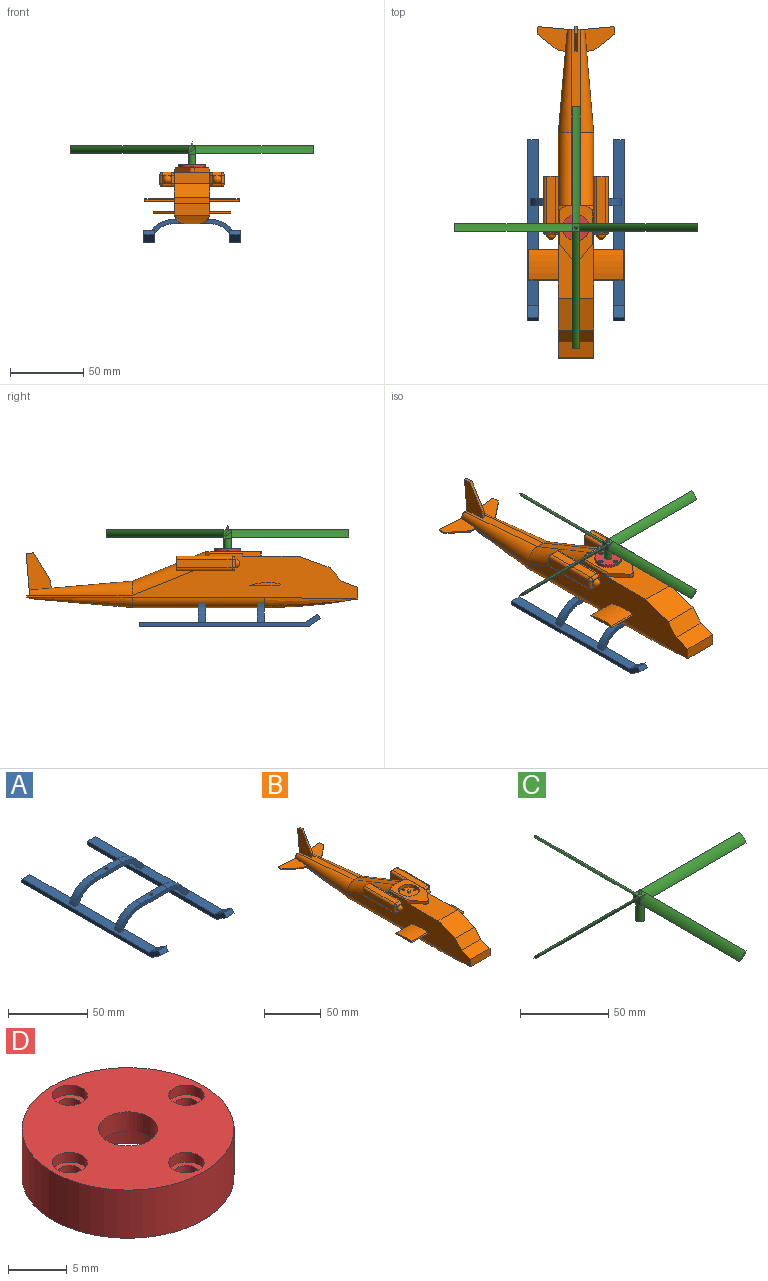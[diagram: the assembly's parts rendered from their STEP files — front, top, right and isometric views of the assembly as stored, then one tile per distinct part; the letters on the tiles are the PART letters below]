
ASSEMBLY  parts=4 mates=3
PART A: 38 faces, bbox 65.5x123.3x16 mm
  f0: cylinder r=20mm len=18.74mm, axis (0,-1,0), area 121.3mm2, adj f1,f6,f7,f8
  f1: plane 24x5mm, normal (0,0,1), area 116.9mm2, adj f0,f2,f6,f7,f35
  f2: cylinder r=20mm len=18.74mm, axis (0,-1,0), area 121.3mm2, adj f1,f6,f7,f9
  f3: cylinder r=17mm len=15.49mm, axis (0,-1,0), area 97.4mm2, adj f4,f6,f7,f9
  f4: plane 24x5mm, normal (0,0,-1), area 112.9mm2, adj f3,f5,f6,f7,f37
  f5: cylinder r=17mm len=15.49mm, axis (0,-1,0), area 97.4mm2, adj f4,f6,f7,f8
  f6: plane 61.47x13mm, normal (0,1,0), area 203.3mm2, adj f0,f1,f2,f3,f4,f5,f8,f9
  f7: plane 61.47x13mm, normal (0,-1,0), area 203.3mm2, adj f0,f1,f2,f3,f4,f5,f8,f9
  f8: plane 113x7mm, normal (0,0,1), area 758.6mm2, adj f0,f5,f6,f7,f10,f15,f16,f17
  f9: plane 113x7mm, normal (0,0,1), area 758.6mm2, adj f2,f3,f6,f7,f12,f13,f16,f17
  f10: cylinder r=20mm len=18.74mm, axis (0,1,0), area 121.3mm2, adj f8,f11,f16,f17
  f11: plane 24x5mm, normal (0,0,1), area 116.9mm2, adj f10,f12,f16,f17,f32
  f12: cylinder r=20mm len=18.74mm, axis (0,1,0), area 121.3mm2, adj f9,f11,f16,f17
  f13: cylinder r=17mm len=15.49mm, axis (0,1,0), area 97.4mm2, adj f9,f14,f16,f17
  f14: plane 24x5mm, normal (0,0,-1), area 112.9mm2, adj f13,f15,f16,f17,f34
  f15: cylinder r=17mm len=15.49mm, axis (0,1,0), area 97.4mm2, adj f8,f14,f16,f17
  f16: plane 61.47x13mm, normal (0,-1,0), area 203.3mm2, adj f8,f9,f10,f11,f12,f13,f14,f15
  f17: plane 61.47x13mm, normal (0,1,0), area 203.3mm2, adj f8,f9,f10,f11,f12,f13,f14,f15
  f18: plane 123.32x8.55mm, normal (-1,0,0), area 378.1mm2, adj f8,f19,f21,f26,f27,f28
  f19: plane 115x7mm, normal (0,0,-1), area 805mm2, adj f18,f20,f21,f26
  f20: plane 123.32x8.55mm, normal (1,0,0), area 378.1mm2, adj f8,f19,f21,f26,f27,f28
  f21: plane 7x3mm, normal (0,1,0), area 21mm2, adj f8,f18,f19,f20
  f22: plane 115x7mm, normal (0,0,-1), area 805mm2, adj f23,f24,f25,f30
  f23: plane 123.32x8.55mm, normal (1,0,0), area 378.1mm2, adj f9,f22,f25,f29,f30,f31
  f24: plane 123.32x8.55mm, normal (-1,0,0), area 378.1mm2, adj f9,f22,f25,f29,f30,f31
  f25: plane 7x3mm, normal (0,1,0), area 21mm2, adj f9,f22,f23,f24
  f26: plane 8.32x7mm, normal (0,-0.55,-0.83), area 70mm2, adj f18,f19,f20,f28
  f27: plane 8.32x7mm, normal (0,0.55,0.83), area 70mm2, adj f8,f18,f20,f28
  f28: plane 7x3mm, normal (0,-0.83,0.55), area 25.2mm2, adj f18,f20,f26,f27
  f29: plane 8.32x7mm, normal (0,0.55,0.83), area 70mm2, adj f9,f23,f24,f31
  f30: plane 8.32x7mm, normal (0,-0.55,-0.83), area 70mm2, adj f22,f23,f24,f31
  f31: plane 7x3mm, normal (0,-0.83,0.55), area 25.2mm2, adj f23,f24,f29,f30
  f32: cylinder r=1mm len=2mm, axis (0,0,-1), area 12.6mm2, adj f11,f33
  f33: plane 3x3mm, normal (0,0,-1), area 3.9mm2, adj f32,f34
  f34: cylinder r=1.5mm len=3mm, axis (0,0,-1), area 9.4mm2, adj f14,f33
  f35: cylinder r=1mm len=2mm, axis (0,0,-1), area 12.6mm2, adj f1,f36
  f36: plane 3x3mm, normal (0,0,-1), area 3.9mm2, adj f35,f37
  f37: cylinder r=1.5mm len=3mm, axis (0,0,-1), area 9.4mm2, adj f4,f36
PART B: 133 faces, bbox 65.5x239.2x39.5 mm
  f0: plane 35x10mm, normal (0,0,-1), area 350mm2, adj f2,f3,f110,f114
  f1: plane 45x10mm, normal (0,0,-1), area 450mm2, adj f2,f3,f33,f111
  f2: cylinder r=7mm len=90mm, axis (0,-1,0), area 922.2mm2, adj f0,f1,f8,f17,f32,f110,f111,f112
  f3: cylinder r=7mm len=90mm, axis (0,-1,0), area 922.2mm2, adj f0,f1,f4,f27,f34,f110,f111,f112
  f4: plane 153.65x31.31mm, normal (-1,0,0), area 3016.8mm2, adj f3,f5,f9,f11,f12,f13,f14,f27
  f5: plane 70x6.12mm, normal (-1,0.09,0), area 76.8mm2, adj f4,f34,f35,f37,f83,f84
  f6: plane 70x6.12mm, normal (0,0.09,1), area 391.6mm2, adj f24,f35,f36,f37,f72,f73,f74
  f7: plane 70x6.12mm, normal (1,0.09,0), area 76.8mm2, adj f8,f32,f36,f37,f65,f68
  f8: plane 153.65x31.31mm, normal (1,0,0), area 3016.8mm2, adj f2,f7,f9,f11,f12,f13,f14,f17
  f9: plane 38.05x24mm, normal (0,0,1), area 742.4mm2, adj f4,f8,f11,f18,f19,f28
  f10: plane 18x18mm, normal (0,0,1), area 237.9mm2, adj f20,f121,f123,f125,f127,f128,f129,f130
  f11: plane 24x21.61mm, normal (0,-0.34,0.94), area 552mm2, adj f4,f8,f9,f12
  f12: plane 24x9.19mm, normal (0,-0.77,0.64), area 288mm2, adj f4,f8,f11,f13
  f13: plane 24x11.28mm, normal (0,-0.34,0.94), area 288mm2, adj f4,f8,f12,f14
  f14: plane 24x8mm, normal (0,-1,0), area 192mm2, adj f4,f8,f13,f15
  f15: cylinder r=350mm len=63.65mm, axis (-1,0,0), area 1088.2mm2, adj f14,f17,f27,f113
  f16: plane 11.21x10.51mm, normal (0,1,0), area 5mm2, adj f21,f23,f25,f42
  f17: bspline ~63.65x7mm, area 424.1mm2, adj f2,f8,f15,f113
  f18: cylinder r=2.5mm len=3.84mm, axis (0,0,-1), area 13.1mm2, adj f9,f19,f21,f28
  f19: plane 12.1x10.08mm, normal (0.77,-0.64,0), area 46.5mm2, adj f8,f9,f18,f21,f22
  f20: cylinder r=9mm len=18mm, axis (0,0,-1), area 169.6mm2, adj f10,f21
  f21: plane 38x22mm, normal (0,0,1), area 452.4mm2, adj f16,f18,f19,f20,f22,f23,f24,f26
  f22: plane 23.2x1mm, normal (0.71,0,0.71), area 32mm2, adj f8,f19,f21,f23
  f23: plane 5.24x5.24mm, normal (0.5,0.71,0.5), area 18.7mm2, adj f8,f16,f21,f22,f42
  f24: plane 50x20mm, normal (0,0.37,0.93), area 323.1mm2, adj f6,f21,f25,f31
  f25: cylinder r=9mm len=56.69mm, axis (0,0.93,-0.37), area 761.3mm2, adj f8,f16,f24,f36,f42
  f26: plane 11.21x10.51mm, normal (0,1,0), area 5mm2, adj f21,f30,f31,f87
  f27: bspline ~63.65x7mm, area 424.1mm2, adj f3,f4,f15,f113
  f28: plane 12.1x10.08mm, normal (-0.77,-0.64,0), area 46.5mm2, adj f4,f9,f18,f21,f29
  f29: plane 23.2x1mm, normal (-0.71,0,0.71), area 32mm2, adj f4,f21,f28,f30
  f30: plane 5.24x5.24mm, normal (-0.5,0.71,0.5), area 18.7mm2, adj f4,f21,f26,f29,f87
  f31: cylinder r=9mm len=56.69mm, axis (0,0.93,-0.37), area 761.3mm2, adj f4,f24,f26,f35,f87
  f32: cone r=7mm half-angle=5deg, axis (0,-1,0), area 434.6mm2, adj f2,f7,f33,f37,f66
  f33: plane 70x10mm, normal (0,0.09,-1), area 702.7mm2, adj f1,f32,f34,f37
  f34: cone r=7mm half-angle=5deg, axis (0,-1,0), area 434.6mm2, adj f3,f5,f33,f37,f86
  f35: bspline ~84x12.21mm, area 694mm2, adj f5,f6,f31,f37
  f36: bspline ~84x12.21mm, area 694mm2, adj f6,f7,f25,f37
  f37: plane 12.56x6.56mm, normal (0,1,0), area 62.8mm2, adj f5,f6,f7,f32,f33,f34,f35,f36
  f38: cylinder r=0.7mm len=20mm, axis (-1,0,0), area 41.4mm2, adj f8,f39,f40,f41
  f39: plane 20x20mm, normal (0,0,-1), area 400mm2, adj f8,f38,f40,f41
  f40: cylinder r=40mm len=20.13mm, axis (-1,0,0), area 408mm2, adj f8,f38,f39,f41
  f41: plane 20.7x2.08mm, normal (1,0,0), area 32mm2, adj f38,f39,f40
  f42: plane 20.17x6mm, normal (-1,0,0), area 117.9mm2, adj f16,f23,f25,f49,f53,f59
  f43: plane 3x3mm, normal (0,-1,0), area 1.9mm2, adj f58,f62,f63
  f44: plane 3x3mm, normal (0,-1,0), area 1.9mm2, adj f52,f58,f63
  f45: plane 3x3mm, normal (0,-1,0), area 1.9mm2, adj f52,f57,f63
  f46: plane 38x6mm, normal (0,0,1), area 228mm2, adj f49,f56,f59,f62
  f47: plane 3x3mm, normal (0,-1,0), area 1.9mm2, adj f57,f62,f63
  f48: plane 38x6mm, normal (0,0,-1), area 228mm2, adj f49,f51,f52,f53
  f49: plane 10x10mm, normal (0,1,0), area 68.3mm2, adj f42,f46,f48,f50,f51,f53,f56,f59
  f50: plane 38x6mm, normal (1,0,0), area 228mm2, adj f49,f51,f56,f57
  f51: cylinder r=2mm len=38mm, axis (0,-1,0), area 119.4mm2, adj f48,f49,f50,f54
  f52: cylinder r=2mm len=6mm, axis (-1,0,0), area 18.8mm2, adj f44,f45,f48,f54,f55
  f53: cylinder r=2mm len=38mm, axis (0,1,0), area 119.4mm2, adj f8,f42,f48,f49,f55
  f54: sphere r=2mm, area 6.3mm2, adj f51,f52,f57
  f55: sphere r=2mm, area 6.3mm2, adj f52,f53,f58
  f56: cylinder r=2mm len=38mm, axis (0,1,0), area 119.4mm2, adj f46,f49,f50,f60
  f57: cylinder r=2mm len=6mm, axis (0,0,1), area 18.8mm2, adj f45,f47,f50,f54,f60
  f58: cylinder r=2mm len=6mm, axis (0,0,-1), area 18.8mm2, adj f8,f43,f44,f55,f61
  f59: cylinder r=2mm len=38mm, axis (0,-1,0), area 119.4mm2, adj f8,f42,f46,f49,f61
  f60: sphere r=2mm, area 6.3mm2, adj f56,f57,f62
  f61: sphere r=2mm, area 6.3mm2, adj f58,f59,f62
  f62: cylinder r=2mm len=6mm, axis (1,0,0), area 18.8mm2, adj f43,f46,f47,f60,f61
  f63: sphere r=3mm, area 56.5mm2, adj f43,f44,f45,f47
  f64: sphere r=3mm, area 56.5mm2, adj f49
  f65: plane 4.98x1mm, normal (0.09,-1,0), area 5mm2, adj f7,f66,f68,f70
  f66: plane 20.36x16.69mm, normal (0,0,-1), area 225mm2, adj f32,f65,f67,f69,f70
  f67: plane 19.92x1.74mm, normal (-0.09,1,0), area 20mm2, adj f37,f66,f68,f69
  f68: plane 20.36x16.69mm, normal (0,0,1), area 225mm2, adj f7,f65,f67,f69,f70
  f69: plane 4.98x1mm, normal (1,0.09,0), area 5mm2, adj f66,f67,f68,f70
  f70: plane 14.07x11.27mm, normal (0.63,-0.78,0), area 18mm2, adj f65,f66,f68,f69
  f71: plane 24.91x2.18mm, normal (0,1,-0.09), area 50mm2, adj f37,f72,f74,f75
  f72: plane 25.34x17.12mm, normal (-1,0,0), area 275mm2, adj f6,f71,f73,f75,f76
  f73: plane 4.98x2mm, normal (0,-1,0.09), area 10mm2, adj f6,f72,f74,f76
  f74: plane 25.34x17.12mm, normal (1,0,0), area 275mm2, adj f6,f71,f73,f75,f76
  f75: plane 4.98x2mm, normal (0,0.09,1), area 10mm2, adj f71,f72,f74,f76
  f76: plane 19.05x11.71mm, normal (0,-0.85,0.52), area 44.7mm2, adj f72,f73,f74,f75
  f77: plane 20.7x2.08mm, normal (-1,0,0), area 32mm2, adj f78,f79,f80
  f78: cylinder r=40mm len=20.13mm, axis (1,0,0), area 408mm2, adj f4,f77,f79,f80
  f79: plane 20x20mm, normal (0,0,-1), area 400mm2, adj f4,f77,f78,f80
  f80: cylinder r=0.7mm len=20mm, axis (1,0,0), area 41.4mm2, adj f4,f77,f78,f79
  f81: plane 4.98x1mm, normal (-1,0.09,0), area 5mm2, adj f82,f84,f85,f86
  f82: plane 14.07x11.27mm, normal (-0.63,-0.78,0), area 18mm2, adj f81,f83,f84,f86
  f83: plane 4.98x1mm, normal (-0.09,-1,0), area 5mm2, adj f5,f82,f84,f86
  f84: plane 20.36x16.69mm, normal (0,0,1), area 225mm2, adj f5,f81,f82,f83,f85
  f85: plane 19.92x1.74mm, normal (0.09,1,0), area 20mm2, adj f37,f81,f84,f86
  f86: plane 20.36x16.69mm, normal (0,0,-1), area 225mm2, adj f34,f81,f82,f83,f85
  f87: plane 20.17x6mm, normal (1,0,0), area 117.9mm2, adj f26,f30,f31,f94,f98,f104
  f88: plane 3x3mm, normal (0,-1,0), area 1.9mm2, adj f103,f107,f108
  f89: plane 3x3mm, normal (0,-1,0), area 1.9mm2, adj f97,f103,f108
  f90: plane 3x3mm, normal (0,-1,0), area 1.9mm2, adj f97,f102,f108
  f91: plane 38x6mm, normal (0,0,1), area 228mm2, adj f94,f101,f104,f107
  f92: plane 3x3mm, normal (0,-1,0), area 1.9mm2, adj f102,f107,f108
  f93: plane 38x6mm, normal (0,0,-1), area 228mm2, adj f94,f96,f97,f98
  f94: plane 10x10mm, normal (0,1,0), area 68.3mm2, adj f87,f91,f93,f95,f96,f98,f101,f104
  f95: plane 38x6mm, normal (-1,0,0), area 228mm2, adj f94,f96,f101,f102
  f96: cylinder r=2mm len=38mm, axis (0,-1,0), area 119.4mm2, adj f93,f94,f95,f99
  f97: cylinder r=2mm len=6mm, axis (1,0,0), area 18.8mm2, adj f89,f90,f93,f99,f100
  f98: cylinder r=2mm len=38mm, axis (0,1,0), area 119.4mm2, adj f4,f87,f93,f94,f100
  f99: sphere r=2mm, area 4mm2, adj f96,f97,f102
  f100: sphere r=2mm, area 8.6mm2, adj f97,f98,f103
  f101: cylinder r=2mm len=38mm, axis (0,1,0), area 119.4mm2, adj f91,f94,f95,f105
  f102: cylinder r=2mm len=6mm, axis (0,0,1), area 18.8mm2, adj f90,f92,f95,f99,f105
  f103: cylinder r=2mm len=6mm, axis (0,0,-1), area 18.8mm2, adj f4,f88,f89,f100,f106
  f104: cylinder r=2mm len=38mm, axis (0,-1,0), area 119.4mm2, adj f4,f87,f91,f94,f106
  f105: sphere r=2mm, area 4mm2, adj f101,f102,f107
  f106: sphere r=2mm, area 8.6mm2, adj f103,f104,f107
  f107: cylinder r=2mm len=6mm, axis (-1,0,0), area 18.8mm2, adj f88,f91,f92,f105,f106
  f108: sphere r=3mm, area 56.5mm2, adj f88,f89,f90,f92
  f109: sphere r=3mm, area 56.5mm2, adj f94
  f110: plane 21.49x3mm, normal (0,1,0), area 54.2mm2, adj f0,f2,f3,f112
  f111: plane 21.49x3mm, normal (0,-1,0), area 54.2mm2, adj f1,f2,f3,f112
  f112: plane 21.49x5mm, normal (0,0,-1), area 104.3mm2, adj f2,f3,f110,f111,f119
  f113: plane 21.75x3.26mm, normal (0,1,0), area 54.2mm2, adj f15,f17,f27,f115
  f114: plane 21.49x3mm, normal (0,-1,0), area 54.2mm2, adj f0,f2,f3,f115
  f115: plane 21.49x5mm, normal (0,0,-1), area 104.3mm2, adj f2,f3,f113,f114,f117
  f116: cone r=0mm half-angle=59deg, axis (0,0,-1), area 3.7mm2, adj f117
  f117: cylinder r=1mm len=4mm, axis (0,0,-1), area 25.1mm2, adj f115,f116
  f118: cone r=0mm half-angle=59deg, axis (0,0,-1), area 3.7mm2, adj f119
  f119: cylinder r=1mm len=4mm, axis (0,0,-1), area 25.1mm2, adj f112,f118
  f120: cone r=0mm half-angle=59deg, axis (0,0,1), area 3.7mm2, adj f121
  f121: cylinder r=1mm len=4mm, axis (0,0,1), area 25.1mm2, adj f10,f120
  f122: cone r=0mm half-angle=59deg, axis (0,0,1), area 3.7mm2, adj f123
  f123: cylinder r=1mm len=4mm, axis (0,0,1), area 25.1mm2, adj f10,f122
  f124: cone r=0mm half-angle=59deg, axis (0,0,1), area 3.7mm2, adj f125
  f125: cylinder r=1mm len=4mm, axis (0,0,1), area 25.1mm2, adj f10,f124
  f126: cone r=0mm half-angle=59deg, axis (0,0,1), area 3.7mm2, adj f127
  f127: cylinder r=1mm len=4mm, axis (0,0,1), area 25.1mm2, adj f10,f126
  f128: plane 3x2mm, normal (0,1,0), area 6mm2, adj f10,f129,f131,f132
  f129: plane 3x2mm, normal (-1,0,0), area 6mm2, adj f10,f128,f130,f132
  f130: plane 3x2mm, normal (0,-1,0), area 6mm2, adj f10,f129,f131,f132
  f131: plane 3x2mm, normal (1,0,0), area 6mm2, adj f10,f128,f130,f132
  f132: plane 2x2mm, normal (0,0,1), area 4mm2, adj f128,f129,f130,f131
PART C: 33 faces, bbox 165x165x21 mm
  f0: plane 5x5mm, normal (0,0,-1), area 15.6mm2, adj f18,f28,f29,f30,f31
  f1: plane 2.5x2.5mm, normal (0,0,-1), area 1.3mm2, adj f4,f5,f18
  f2: plane 2.5x2.5mm, normal (0,0,-1), area 1.3mm2, adj f4,f11,f18
  f3: plane 2.5x2.5mm, normal (0,0,-1), area 1.3mm2, adj f7,f11,f18
  f4: plane 6x5mm, normal (0,1,0), area 13.6mm2, adj f1,f2,f5,f9,f11,f27
  f5: plane 6x5mm, normal (-1,0,0), area 13.6mm2, adj f1,f4,f7,f10,f13,f23
  f6: plane 5x5mm, normal (1,0,0), area 8.6mm2, adj f7,f12,f20
  f7: plane 6x5mm, normal (0,-1,0), area 13.6mm2, adj f3,f5,f6,f11,f13,f14
  f8: plane 5x5mm, normal (0,1,0), area 8.6mm2, adj f11,f12,f26
  f9: plane 5x5mm, normal (-1,0,0), area 8.6mm2, adj f4,f12,f24
  f10: plane 5x5mm, normal (0,-1,0), area 8.6mm2, adj f5,f12,f15
  f11: plane 6x5mm, normal (1,0,0), area 13.6mm2, adj f2,f3,f4,f7,f8,f21
  f12: plane 5x5mm, normal (0,0,1), area 21.9mm2, adj f6,f8,f9,f10,f17
  f13: plane 2.5x2.5mm, normal (0,0,-1), area 1.3mm2, adj f5,f7,f18
  f14: cylinder r=8mm len=80mm, axis (0,1,0), area 585.9mm2, adj f7,f15,f16
  f15: cylinder r=8mm len=80mm, axis (0,1,0), area 585.9mm2, adj f10,f14,f16
  f16: plane 5x5mm, normal (0,-1,0), area 7.8mm2, adj f14,f15
  f17: cone r=1mm half-angle=18.4deg, axis (0,0,-1), area 9.9mm2, adj f12
  f18: cylinder r=2.5mm len=12mm, axis (0,0,1), area 188.5mm2, adj f0,f1,f2,f3,f13
  f19: plane 5x5mm, normal (1,0,0), area 7.8mm2, adj f20,f21
  f20: cylinder r=8mm len=80mm, axis (-1,0,0), area 585.9mm2, adj f6,f19,f21
  f21: cylinder r=8mm len=80mm, axis (-1,0,0), area 585.9mm2, adj f11,f19,f20
  f22: plane 5x5mm, normal (-1,0,0), area 7.8mm2, adj f23,f24
  f23: cylinder r=8mm len=80mm, axis (1,0,0), area 585.9mm2, adj f5,f22,f24
  f24: cylinder r=8mm len=80mm, axis (1,0,0), area 585.9mm2, adj f9,f22,f23
  f25: plane 5x5mm, normal (0,1,0), area 7.8mm2, adj f26,f27
  f26: cylinder r=8mm len=80mm, axis (0,-1,0), area 585.9mm2, adj f8,f25,f27
  f27: cylinder r=8mm len=80mm, axis (0,-1,0), area 585.9mm2, adj f4,f25,f26
  f28: plane 3x2mm, normal (0,1,0), area 6mm2, adj f0,f29,f31,f32
  f29: plane 3x2mm, normal (1,0,0), area 6mm2, adj f0,f28,f30,f32
  f30: plane 3x2mm, normal (0,-1,0), area 6mm2, adj f0,f29,f31,f32
  f31: plane 3x2mm, normal (-1,0,0), area 6mm2, adj f0,f28,f30,f32
  f32: plane 2x2mm, normal (0,0,-1), area 4mm2, adj f28,f29,f30,f31
PART D: 18 faces, bbox 18x18x5 mm
  f0: cylinder r=9mm len=18mm, axis (0,0,-1), area 282.7mm2, adj f1,f2
  f1: plane 18x18mm, normal (0,0,1), area 206.6mm2, adj f0,f3,f8,f11,f14,f17
  f2: plane 18x18mm, normal (0,0,-1), area 163.4mm2, adj f0,f4,f6,f9,f12,f15
  f3: cylinder r=2.5mm len=5mm, axis (0,0,-1), area 31.4mm2, adj f1,f5
  f4: cylinder r=5mm len=10mm, axis (0,0,-1), area 94.2mm2, adj f2,f5
  f5: plane 10x10mm, normal (0,0,-1), area 58.9mm2, adj f3,f4
  f6: cylinder r=1mm len=4mm, axis (0,0,1), area 25.1mm2, adj f2,f7
  f7: plane 3x3mm, normal (0,0,1), area 3.9mm2, adj f6,f8
  f8: cylinder r=1.5mm len=3mm, axis (0,0,1), area 9.4mm2, adj f1,f7
  f9: cylinder r=1mm len=4mm, axis (0,0,1), area 25.1mm2, adj f2,f10
  f10: plane 3x3mm, normal (0,0,1), area 3.9mm2, adj f9,f11
  f11: cylinder r=1.5mm len=3mm, axis (0,0,1), area 9.4mm2, adj f1,f10
  f12: cylinder r=1mm len=4mm, axis (0,0,1), area 25.1mm2, adj f2,f13
  f13: plane 3x3mm, normal (0,0,1), area 3.9mm2, adj f12,f14
  f14: cylinder r=1.5mm len=3mm, axis (0,0,1), area 9.4mm2, adj f1,f13
  f15: cylinder r=1mm len=4mm, axis (0,0,1), area 25.1mm2, adj f2,f16
  f16: plane 3x3mm, normal (0,0,1), area 3.9mm2, adj f15,f17
  f17: cylinder r=1.5mm len=3mm, axis (0,0,1), area 9.4mm2, adj f1,f16
PLACE A t=(16.64,-18.43,-46.44)mm
PLACE B t=(16.64,-18.43,-46.44)mm
PLACE C rot(axis=(0,0,1),90deg) t=(16.64,-33.43,1.56)mm
PLACE D t=(16.64,-33.43,-11.44)mm
MATE revolute C.f18 <-> B.f20  axis (0,0,-1) through (16.64,-33.43,-11.44)mm
MATE fastened D.f0 <-> B.f20  axis (0,0,-1) through (16.64,-33.43,-11.44)mm
MATE fastened A.f32 <-> B.f116  axis (0,0,1) through (16.64,-55.93,-43.44)mm
